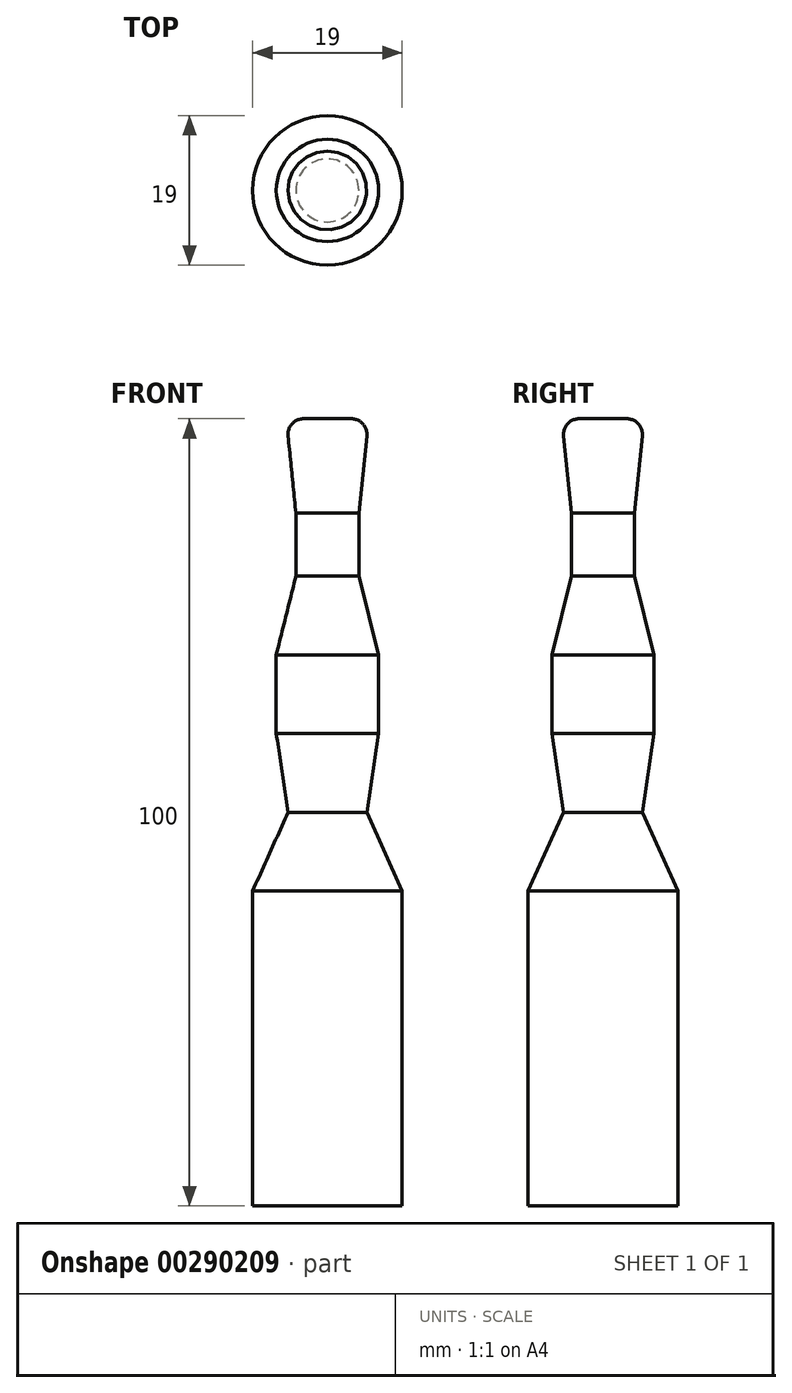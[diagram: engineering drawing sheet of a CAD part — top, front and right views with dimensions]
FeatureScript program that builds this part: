
annotation { "Feature Type Name" : "Feature", "Feature Type Description" : "" }
export const myFeature = defineFeature(function(context is Context, id is Id, definition is map)
    precondition{}
    {
        {
            var Q0;
            Q0=qCreatedBy(makeId("Front.planeOp"),FACE);
            var sketch = newSketch(context, id + "F0", { "sketchPlane" : qUnion([Q0])});
            skLineSegment(sketch, "E0", {"start": v(0, 0) * mm, "end": v(3.01, 0) * mm});
            skLineSegment(sketch, "E1", {"start": v(4, -12) * mm, "end": v(4, -20) * mm});
            skLineSegment(sketch, "E2", {"start": v(4, -20) * mm, "end": v(6.5, -30) * mm});
            skLineSegment(sketch, "E3", {"start": v(6.5, -30) * mm, "end": v(6.5, -40) * mm});
            skLineSegment(sketch, "E4", {"start": v(6.5, -40) * mm, "end": v(5, -50) * mm});
            skLineSegment(sketch, "E5", {"start": v(5, -50) * mm, "end": v(9.5, -60) * mm});
            skLineSegment(sketch, "E6", {"start": v(9.5, -60) * mm, "end": v(9.5, -100) * mm});
            skLineSegment(sketch, "E7", {"start": v(9.5, -100) * mm, "end": v(0, -100) * mm});
            skLineSegment(sketch, "E8", {"start": v(0, -100) * mm, "end": v(0, 0) * mm});
            skArc(sketch, "E9", {"start": v(5, -2.2) * mm, "mid": v(4.5, -0.66) * mm, "end": v(3.01, 0) * mm});
            skLineSegment(sketch, "E10", {"start": v(5, -2.2) * mm, "end": v(4, -12) * mm});
            skSolve(sketch);
        }
        {
            var Q0;
            Q0=makeQuery(id+"F0.imprint","IMPRINT",FACE,{"disambiguationData":[TD([[makeQuery(id+"F0.imprint","IMPRINT",EDGE,{"derivedFrom":sQuery(id+"F0.wireOp",EDGE,"E0")}),-1.0]])]});
            var Q1;
            Q1=sQuery(id+"F0.wireOp",EDGE,"E8");
            revolve(context, id + "F1", {"entities" : qUnion([Q0]), "axis" : qUnion([Q1]), "revolveType" : RevolveType.FULL});
        }
    });
